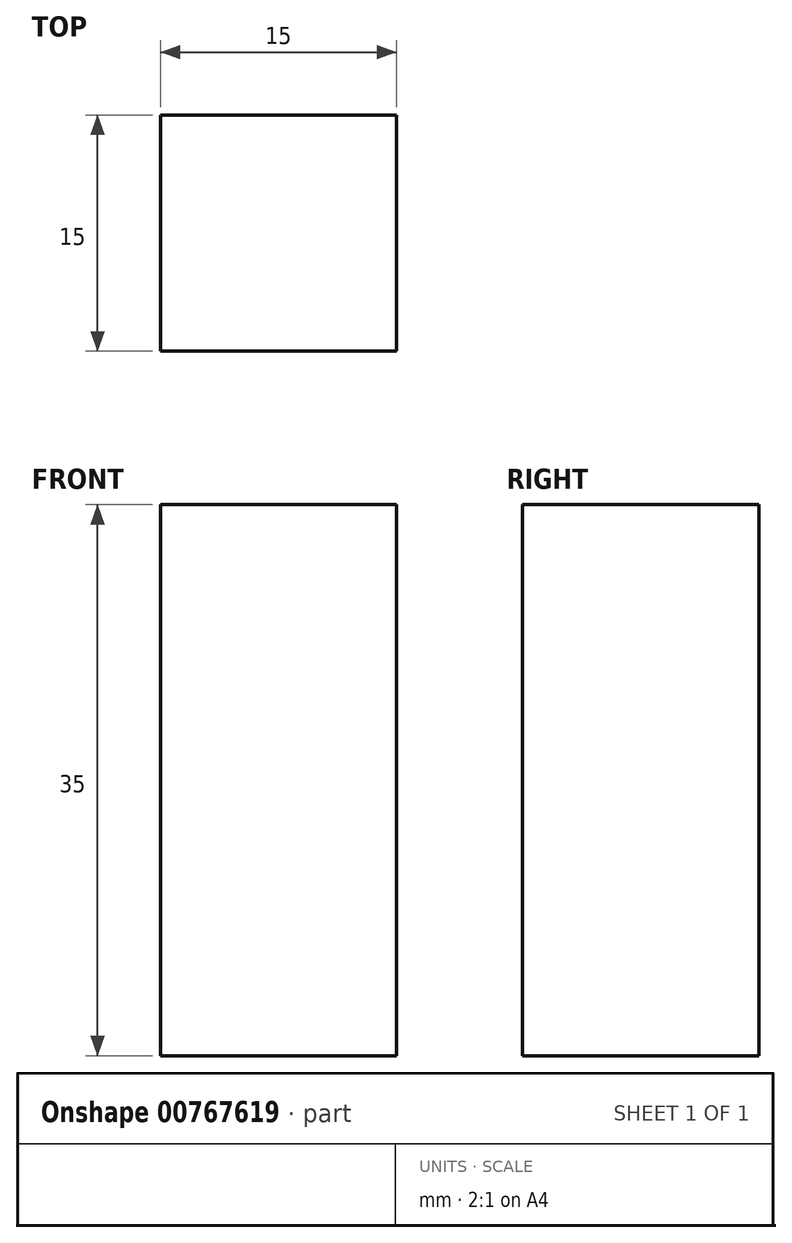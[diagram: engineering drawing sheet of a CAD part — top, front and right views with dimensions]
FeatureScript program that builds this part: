
annotation { "Feature Type Name" : "Feature", "Feature Type Description" : "" }
export const myFeature = defineFeature(function(context is Context, id is Id, definition is map)
    precondition{}
    {
        {
            var Q0;
            Q0=qCreatedBy(makeId("Top.planeOp"),FACE);
            var sketch = newSketch(context, id + "F0", { "sketchPlane" : qUnion([Q0])});
            skLineSegment(sketch, "E0.bottom", {"start": v(0, 0) * mm, "end": v(15, 0) * mm});
            skLineSegment(sketch, "E0.top", {"start": v(0, 15) * mm, "end": v(15, 15) * mm});
            skLineSegment(sketch, "E0.left", {"start": v(0, 0) * mm, "end": v(0, 15) * mm});
            skLineSegment(sketch, "E0.right", {"start": v(15, 0) * mm, "end": v(15, 15) * mm});
            skSolve(sketch);
        }
        {
            var Q0;
            Q0 = qSketchRegion(id + "F0", true);
            extrude(context, id + "F1", {"entities" : qUnion([Q0]), "depth" : 35 * mm, "offsetDistance" : 25.4 * mm});
        }
    });
